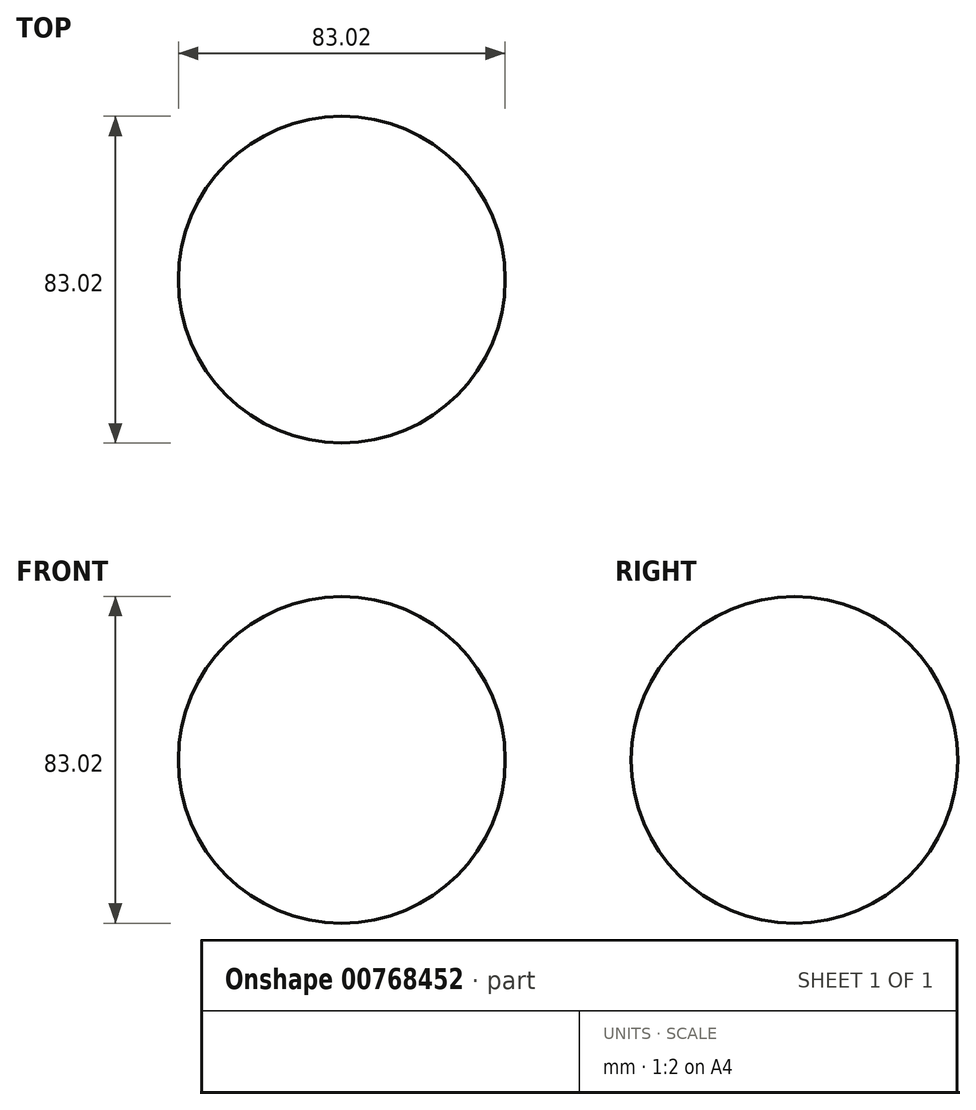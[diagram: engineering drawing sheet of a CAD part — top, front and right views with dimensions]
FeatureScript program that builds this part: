
annotation { "Feature Type Name" : "Feature", "Feature Type Description" : "" }
export const myFeature = defineFeature(function(context is Context, id is Id, definition is map)
    precondition{}
    {
        {
            var Q0;
            Q0=qCreatedBy(makeId("Top.planeOp"),FACE);
            var sketch = newSketch(context, id + "F0", { "sketchPlane" : qUnion([Q0])});
            skCircle(sketch, "E0", {"center": v(0, 0) * mm, "radius": 41.51 * mm});
            skLineSegment(sketch, "E1", {"start": v(0, 41.51) * mm, "end": v(0, -41.51) * mm});
            skSolve(sketch);
        }
        {
            var Q0;
            {var subQ0=sQuery(id+"F0.wireOp",EDGE,"E1");Q0=makeQuery(id+"F0.imprint","IMPRINT",FACE,{"disambiguationData":[TD([[makeQuery(id+"F0.imprint","IMPRINT",EDGE,{"derivedFrom":subQ0}),1.0]])]});}
            var Q1;
            Q1=sQuery(id+"F0.wireOp",EDGE,"E1");
            revolve(context, id + "F1", {"surfaceOperationType" : NewSurfaceOperationType.NEW, "entities" : qUnion([Q0]), "axis" : qUnion([Q1]), "revolveType" : RevolveType.FULL});
        }
    });
